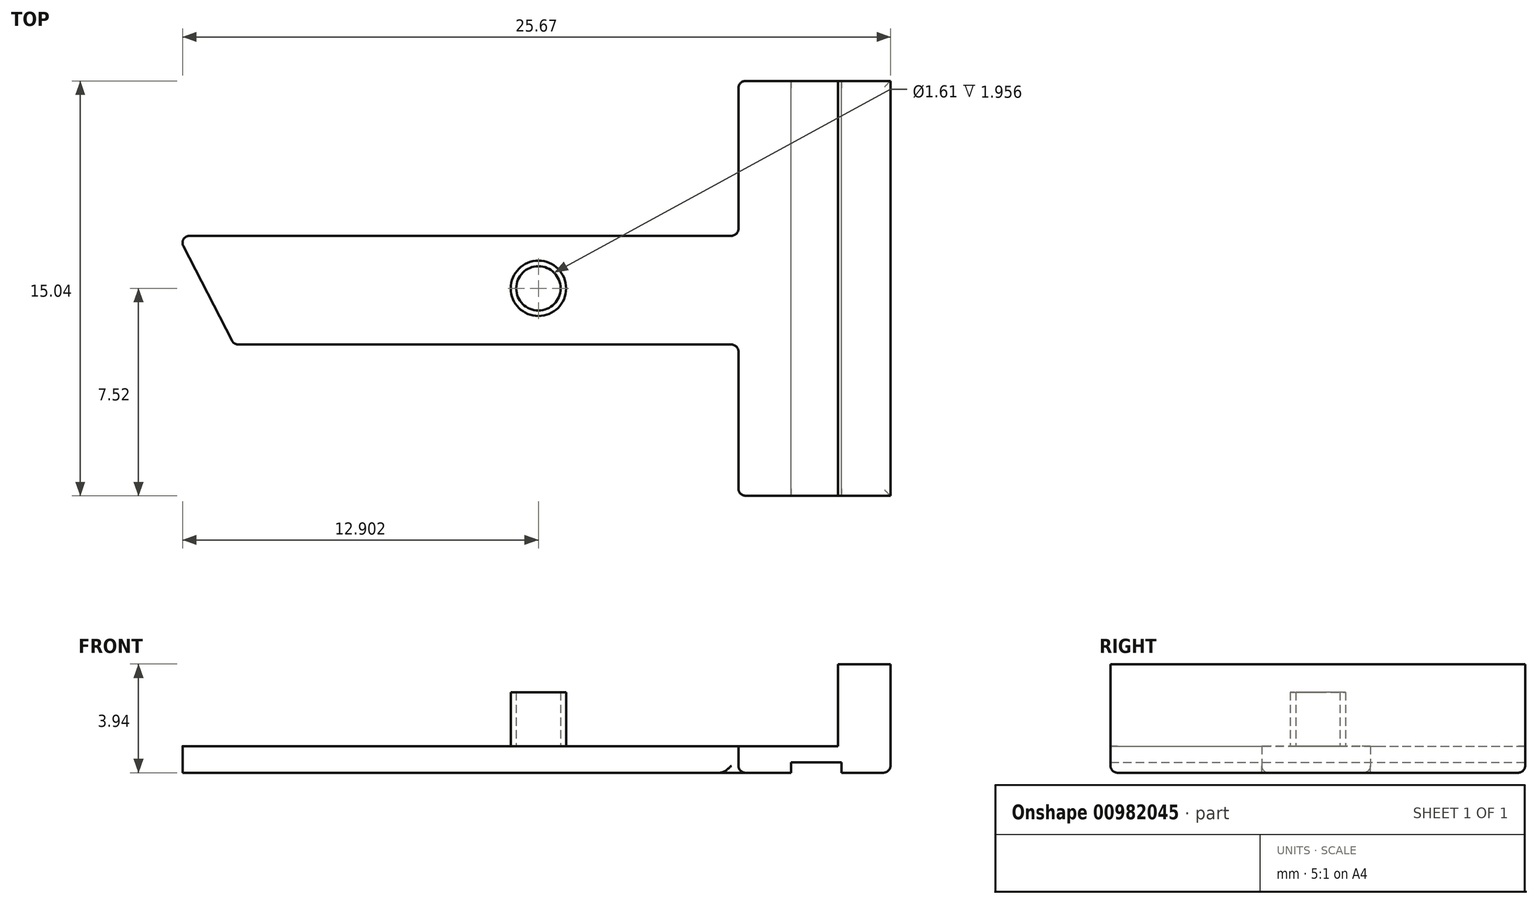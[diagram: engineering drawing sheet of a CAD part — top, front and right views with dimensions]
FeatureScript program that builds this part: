
annotation { "Feature Type Name" : "Feature", "Feature Type Description" : "" }
export const myFeature = defineFeature(function(context is Context, id is Id, definition is map)
    precondition{}
    {
        {
            var Q0;
            Q0=qCreatedBy(makeId("Top.planeOp"),FACE);
            var sketch = newSketch(context, id + "F0", { "sketchPlane" : qUnion([Q0])});
            skLineSegment(sketch, "E0.bottom", {"start": v(2.76, -7.52) * mm, "end": v(-2.76, -7.52) * mm});
            skLineSegment(sketch, "E0.top", {"start": v(2.76, 7.52) * mm, "end": v(0.85, 7.52) * mm});
            skLineSegment(sketch, "E0.left", {"start": v(2.76, -7.52) * mm, "end": v(2.76, 7.52) * mm});
            skLineSegment(sketch, "E0.right", {"start": v(-2.76, -7.52) * mm, "end": v(-2.76, -2.04) * mm});
            skPoint(sketch, "E0.middle", {"position": v(0, 0) * mm});
            skLineSegment(sketch, "E1.bottom", {"start": v(-2.76, 1.9) * mm, "end": v(-23.08, 1.9) * mm});
            skLineSegment(sketch, "E1.top", {"start": v(-2.76, -2.04) * mm, "end": v(-21.04, -2.04) * mm});
            skLineSegment(sketch, "E2", {"start": v(-23.08, 1.9) * mm, "end": v(-21.04, -2.04) * mm});
            skLineSegment(sketch, "E3.trimOffspring", {"start": v(-2.76, 1.9) * mm, "end": v(-2.76, 7.52) * mm});
            skLineSegment(sketch, "E4", {"start": v(0.85, 7.52) * mm, "end": v(-2.76, 7.52) * mm});
            skSolve(sketch);
        }
        {
            var Q0;
            Q0 = qSketchRegion(id + "F0", true);
            extrude(context, id + "F1", {"entities" : qUnion([Q0]), "depth" : 0.97 * mm, "offsetDistance" : 25.4 * mm});
        }
        {
            var Q0;
            Q0=makeQuery(id+"F1.opExtrude","CAP_FACE",FACE,{"disambiguationData":[OSD([sQuery(id+"F0.wireOp",EDGE,"E0.bottom"),sQuery(id+"F0.wireOp",EDGE,"E0.top"),sQuery(id+"F0.wireOp",EDGE,"E0.left"),sQuery(id+"F0.wireOp",EDGE,"E0.right"),sQuery(id+"F0.wireOp",EDGE,"E1.bottom"),sQuery(id+"F0.wireOp",EDGE,"E1.top"),sQuery(id+"F0.wireOp",EDGE,"E2"),sQuery(id+"F0.wireOp",EDGE,"E3.trimOffspring"),sQuery(id+"F0.wireOp",EDGE,"E4")])],"isStart":false});
            var sketch = newSketch(context, id + "F2", { "sketchPlane" : qUnion([Q0])});
            skLineSegment(sketch, "E5.bottom", {"start": v(2.76, -7.52) * mm, "end": v(0.85, -7.52) * mm});
            skLineSegment(sketch, "E5.top", {"start": v(2.76, 7.52) * mm, "end": v(0.85, 7.52) * mm});
            skLineSegment(sketch, "E5.left", {"start": v(2.76, -7.52) * mm, "end": v(2.76, 7.52) * mm});
            skLineSegment(sketch, "E5.right", {"start": v(0.85, -7.52) * mm, "end": v(0.85, 7.52) * mm});
            skCircle(sketch, "E6", {"center": v(-10, 0) * mm, "radius": 1 * mm});
            skCircle(sketch, "E7", {"center": v(-10, 0) * mm, "radius": 0.8 * mm});
            skSolve(sketch);
        }
        {
            var Q0;
            Q0=makeQuery(id+"F2.imprint","IMPRINT",FACE,{"disambiguationData":[TD([[makeQuery(id+"F2.imprint","IMPRINT",EDGE,{"derivedFrom":sQuery(id+"F2.wireOp",EDGE,"E5.bottom")}),-1.0]])]});
            extrude(context, id + "F3", {"entities" : qUnion([Q0]), "operationType" : NewBodyOperationType.ADD, "depth" : 2.97 * mm, "offsetDistance" : 25.4 * mm});
        }
        {
            var Q0;
            Q0=makeQuery(id+"F2.imprint","IMPRINT",FACE,{"disambiguationData":[TD([[makeQuery(id+"F2.imprint","IMPRINT",EDGE,{"derivedFrom":sQuery(id+"F2.wireOp",EDGE,"E6")}),1.0]])]});
            extrude(context, id + "F4", {"entities" : qUnion([Q0]), "operationType" : NewBodyOperationType.ADD, "depth" : 1.96 * mm, "offsetDistance" : 25.4 * mm});
        }
        {
            var Q0;
            Q0=makeQuery(id+"F1.opExtrude","CAP_FACE",FACE,{"disambiguationData":[OSD([sQuery(id+"F0.wireOp",EDGE,"E0.bottom"),sQuery(id+"F0.wireOp",EDGE,"E0.top"),sQuery(id+"F0.wireOp",EDGE,"E0.left"),sQuery(id+"F0.wireOp",EDGE,"E0.right"),sQuery(id+"F0.wireOp",EDGE,"E1.bottom"),sQuery(id+"F0.wireOp",EDGE,"E1.top"),sQuery(id+"F0.wireOp",EDGE,"E2"),sQuery(id+"F0.wireOp",EDGE,"E3.trimOffspring"),sQuery(id+"F0.wireOp",EDGE,"E4")])],"isStart":true});
            var sketch = newSketch(context, id + "F5", { "sketchPlane" : qUnion([Q0])});
            skLineSegment(sketch, "E8.bottom", {"start": v(-0.85, 7.52) * mm, "end": v(0.98, 7.52) * mm});
            skLineSegment(sketch, "E8.top", {"start": v(-0.85, -7.52) * mm, "end": v(0.98, -7.52) * mm});
            skLineSegment(sketch, "E8.left", {"start": v(-0.85, 7.52) * mm, "end": v(-0.85, -7.52) * mm});
            skLineSegment(sketch, "E8.right", {"start": v(0.98, 7.52) * mm, "end": v(0.98, -7.52) * mm});
            skSolve(sketch);
        }
        {
            var Q0;
            Q0=makeQuery(id+"F5.imprint","IMPRINT",FACE,{"disambiguationData":[TD([[makeQuery(id+"F5.imprint","IMPRINT",EDGE,{"derivedFrom":sQuery(id+"F5.wireOp",EDGE,"E8.bottom")}),1.0]])]});
            extrude(context, id + "F6", {"entities" : qUnion([Q0]), "operationType" : NewBodyOperationType.REMOVE, "oppositeDirection" : true, "depth" : 0.38 * mm, "offsetDistance" : 25.4 * mm});
        }
        {
            var Q0;
            Q0=makeQuery(id+"F1.opExtrude","SWEPT_EDGE",EDGE,{"disambiguationData":[OSD([sQuery(id+"F0.wireOp",EDGE,"E1.bottom"),sQuery(id+"F0.wireOp",EDGE,"E2")])]});
            var Q1;
            Q1=makeQuery(id+"F1.opExtrude","SWEPT_EDGE",EDGE,{"disambiguationData":[OSD([sQuery(id+"F0.wireOp",EDGE,"E1.top"),sQuery(id+"F0.wireOp",EDGE,"E2")])]});
            var Q2;
            Q2=makeQuery(id+"F1.opExtrude","SWEPT_EDGE",EDGE,{"disambiguationData":[OSD([sQuery(id+"F0.wireOp",EDGE,"E0.bottom"),sQuery(id+"F0.wireOp",EDGE,"E0.right")])]});
            var Q3;
            Q3=makeQuery(id+"F1.opExtrude","SWEPT_EDGE",EDGE,{"disambiguationData":[OSD([sQuery(id+"F0.wireOp",EDGE,"E3.trimOffspring"),sQuery(id+"F0.wireOp",EDGE,"E4")])]});
            var Q4;
            Q4=makeQuery(id+"F1.opExtrude","SWEPT_EDGE",EDGE,{"disambiguationData":[OSD([sQuery(id+"F0.wireOp",EDGE,"E0.right"),sQuery(id+"F0.wireOp",EDGE,"E1.top")])]});
            var Q5;
            Q5=makeQuery(id+"F1.opExtrude","SWEPT_EDGE",EDGE,{"disambiguationData":[OSD([sQuery(id+"F0.wireOp",EDGE,"E1.bottom"),sQuery(id+"F0.wireOp",EDGE,"E3.trimOffspring")])]});
            var Q6;
            {var subQ0=sQuery(id+"F0.wireOp",EDGE,"E3.trimOffspring");var subQ1=sQuery(id+"F0.wireOp",EDGE,"E4");var subQ2=sQuery(id+"F0.wireOp",EDGE,"E0.top");Q6=makeQuery(id+"F6.boolean.opBoolean","SPLIT",EDGE,{"disambiguationData":[TD([makeQuery(id+"F1.opExtrude","SWEPT_FACE",FACE,{"disambiguationData":[OSD([subQ0])]})])],"derivedFrom":makeQuery(id+"F1.opExtrude","CAP_EDGE",EDGE,{"disambiguationData":[OSD([subQ2,subQ1])],"isStart":true})});}
            var Q7;
            {var subQ0=sQuery(id+"F0.wireOp",EDGE,"E0.left");var subQ1=sQuery(id+"F0.wireOp",EDGE,"E4");var subQ2=sQuery(id+"F0.wireOp",EDGE,"E0.top");Q7=makeQuery(id+"F6.boolean.opBoolean","SPLIT",EDGE,{"disambiguationData":[TD([makeQuery(id+"F1.opExtrude","SWEPT_FACE",FACE,{"disambiguationData":[OSD([subQ0])]})])],"derivedFrom":makeQuery(id+"F1.opExtrude","CAP_EDGE",EDGE,{"disambiguationData":[OSD([subQ2,subQ1])],"isStart":true})});}
            var Q8;
            Q8=makeQuery(id+"F1.opExtrude","CAP_EDGE",EDGE,{"disambiguationData":[OSD([sQuery(id+"F0.wireOp",EDGE,"E0.left")])],"isStart":true});
            var Q9;
            Q9=makeQuery(id+"F1.opExtrude","CAP_EDGE",EDGE,{"disambiguationData":[OSD([sQuery(id+"F0.wireOp",EDGE,"E3.trimOffspring")])],"isStart":true});
            var Q10;
            Q10=makeQuery(id+"F1.opExtrude","CAP_EDGE",EDGE,{"disambiguationData":[OSD([sQuery(id+"F0.wireOp",EDGE,"E0.right")])],"isStart":true});
            var Q11;
            {var subQ0=sQuery(id+"F0.wireOp",EDGE,"E0.right");var subQ1=sQuery(id+"F0.wireOp",EDGE,"E0.bottom");Q11=makeQuery(id+"F6.boolean.opBoolean","SPLIT",EDGE,{"disambiguationData":[TD([makeQuery(id+"F1.opExtrude","SWEPT_FACE",FACE,{"disambiguationData":[OSD([subQ0])]})])],"derivedFrom":makeQuery(id+"F1.opExtrude","CAP_EDGE",EDGE,{"disambiguationData":[OSD([subQ1])],"isStart":true})});}
            var Q12;
            {var subQ0=sQuery(id+"F0.wireOp",EDGE,"E0.left");var subQ1=sQuery(id+"F0.wireOp",EDGE,"E0.bottom");Q12=makeQuery(id+"F6.boolean.opBoolean","SPLIT",EDGE,{"disambiguationData":[TD([makeQuery(id+"F1.opExtrude","SWEPT_FACE",FACE,{"disambiguationData":[OSD([subQ0])]})])],"derivedFrom":makeQuery(id+"F1.opExtrude","CAP_EDGE",EDGE,{"disambiguationData":[OSD([subQ1])],"isStart":true})});}
            fillet(context, id + "F7", {"entities" : qUnion([Q0, Q1, Q2, Q3, Q4, Q5, Q6, Q7, Q8, Q9, Q10, Q11, Q12]), "radius" : 0.25 * mm, "tangentPropagation" : true, "allowEdgeOverflow" : false});
        }
    });
